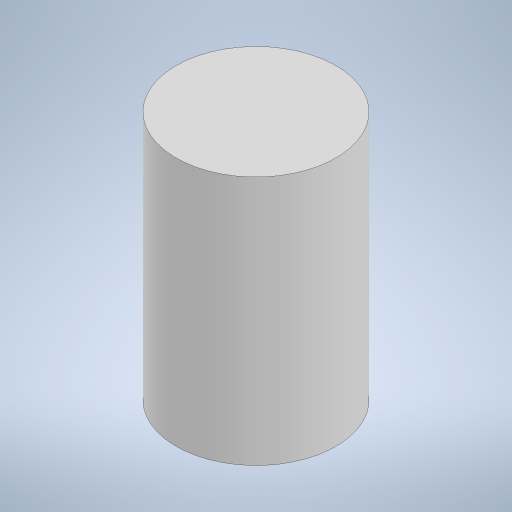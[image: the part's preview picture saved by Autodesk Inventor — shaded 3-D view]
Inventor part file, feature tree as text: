
AUTODESK INVENTOR PART (.ipt)
format: ipt  version: 2024.2 (Build 282272000, 272)  size: 212,480 bytes
history: native  units: mm
features: extrude x1, sketch x1
ambient origin geometry x8: Origin, YZ Plane, XZ Plane, XY Plane, X Axis, Y Axis, Z Axis, Center Point
bodies: Solid1 (feature_tree)
feature tree (2):
  extrude  "Extrusion1"  Depth=5.0mm TaperAngle=0.0deg
  sketch  "Sketch1"  dims[d0=3.2mm d1=5.0mm d2=0.0mm]
